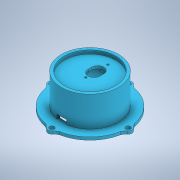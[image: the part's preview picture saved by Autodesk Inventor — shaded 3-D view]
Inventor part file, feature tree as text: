
AUTODESK INVENTOR PART (.ipt)
format: ipt  version: 2021 (Build 250183000, 183)  size: 332,800 bytes
history: native  units: mm
features: extrude x10, projected_geometry x9, sketch x7, other x1
ambient origin geometry x8: Origin, YZ Plane, XZ Plane, XY Plane, X Axis, Y Axis, Z Axis, Center Point
bodies: Body1 (feature_tree)
feature tree (27):
  other  "Sólido1"
  extrude  "Extrusión1"  Depth=5.0mm
  sketch  "Boceto2"  dims[d4=6.0mm d5=5.0mm d6=0.0mm]
  extrude  "Extrusión2"  Depth=5.0mm TaperAngle=0.0deg
  extrude  "Extrusión3"  Depth=12.5mm
  extrude  "Extrusión4"  Depth=5.0mm
  extrude  "Extrusión5"  Depth=54.0mm
  extrude  "Extrusión6"  Depth=3.0mm TaperAngle=0.0deg
  extrude  "Extrusión7"  Depth=6.8mm TaperAngle=0.0deg
  sketch  "Boceto6"  dims[d17=3.0mm d18=3.0mm d19=0.0mm]
  extrude  "Extrusión8"  Depth=12.5mm
  extrude  "Extrusión9"  Depth=5.0mm
  extrude  "Extrusión10"  Depth=12.5mm
  sketch  "Boceto1"  dims[d1=5.0mm d2=2.0mm]
  projected_geometry  "Contorno proyectado1"
  sketch  "Boceto3"  dims[d8=12.5mm d10=12.5mm]
  sketch  "Boceto4"  dims[d12=12.5mm d13=5.0mm]
  sketch  "Boceto5"  dims[d14=2.0mm d15=54.0mm]
  projected_geometry  "Contorno proyectado2"
  projected_geometry  "Contorno proyectado3"
  projected_geometry  "Contorno proyectado4"
  projected_geometry  "Contorno proyectado5"
  sketch  "Boceto7"  dims[d20=5.0mm d21=0.0mm d22=6.8mm d23=0.0mm d24=12.5mm d25=5.0mm d26=12.5mm d27=5.0mm d28=2.0mm d29=2.0mm d30=3.0mm d31=0.0mm d32=60.0mm d33=54.0mm d34=25.0mm d35=0.0mm d36=80.0mm d37=5.0mm d38=10.0mm d39=3.0mm d40=0.0mm d41=8.0mm d42=5.0mm d43=10.0mm d44=10.0mm d45=8.0mm d46=5.0mm d47=10.0mm d48=10.0mm d49=8.0mm d50=5.0mm d51=8.0mm d52=5.0mm d53=10.0mm d54=10.0mm d55=3.0mm d56=0.0mm d57=3.0mm d58=0.0mm d59=5.0mm d60=5.0mm d61=10.0mm d62=10.0mm d63=5.0mm d64=30.0mm d65=0.0mm]
  projected_geometry  "Contorno proyectado6"
  projected_geometry  "Contorno proyectado7"
  projected_geometry  "Contorno proyectado8"
  projected_geometry  "Contorno proyectado9"
